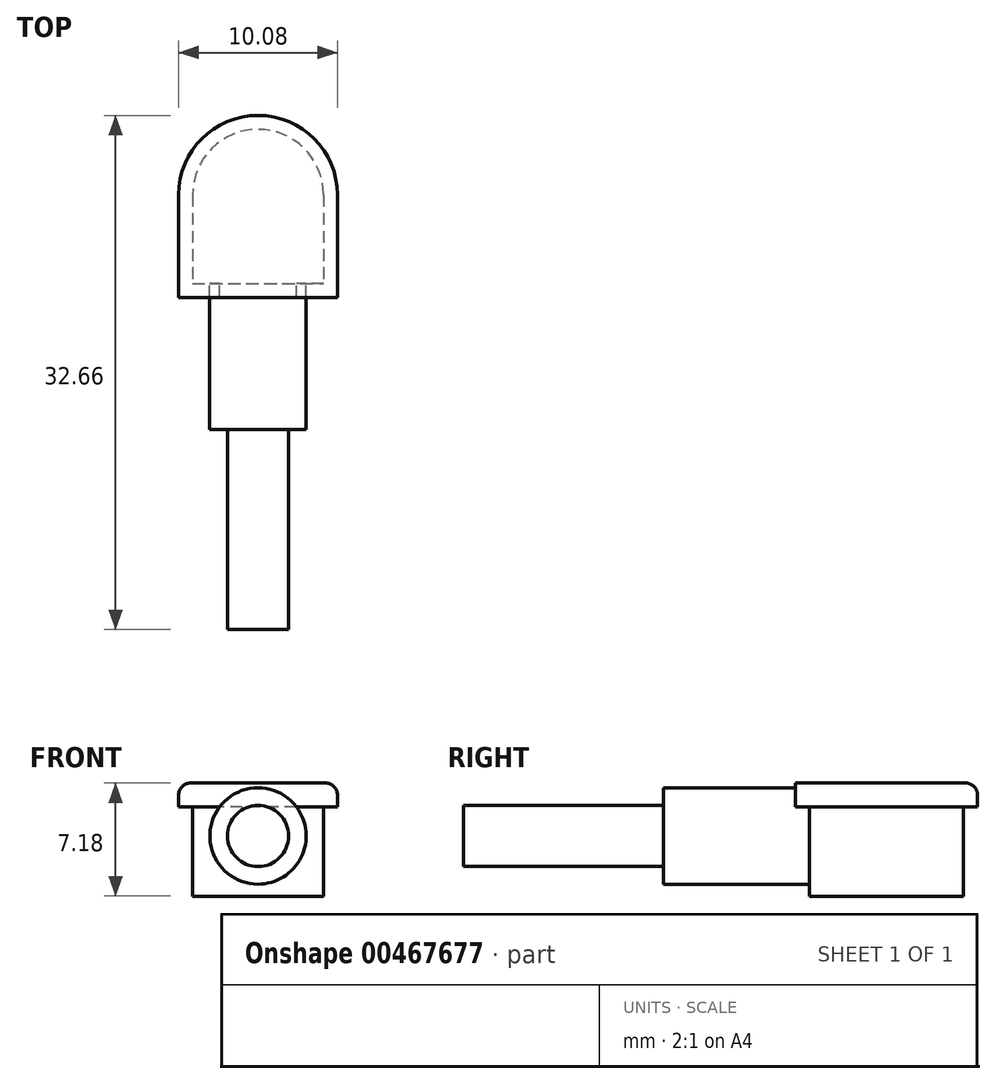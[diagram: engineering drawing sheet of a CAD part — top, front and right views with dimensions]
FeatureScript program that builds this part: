
annotation { "Feature Type Name" : "Feature", "Feature Type Description" : "" }
export const myFeature = defineFeature(function(context is Context, id is Id, definition is map)
    precondition{}
    {
        {
            var Q0;
            Q0=qCreatedBy(makeId("Top.planeOp"),FACE);
            var sketch = newSketch(context, id + "F0", { "sketchPlane" : qUnion([Q0])});
            skArc(sketch, "E0", {"start": v(4.15, 0) * mm, "mid": v(0, 4.15) * mm, "end": v(-4.15, 0) * mm});
            skLineSegment(sketch, "E1.top", {"start": v(-4.15, -5.63) * mm, "end": v(4.15, -5.63) * mm});
            skLineSegment(sketch, "E1.left", {"start": v(-4.15, 0) * mm, "end": v(-4.15, -5.63) * mm});
            skLineSegment(sketch, "E1.right", {"start": v(4.15, 0) * mm, "end": v(4.15, -5.63) * mm});
            skSolve(sketch);
        }
        {
            var Q0;
            Q0 = qSketchRegion(id + "F0", true);
            extrude(context, id + "F1", {"entities" : qUnion([Q0]), "oppositeDirection" : true, "depth" : 5.66 * mm});
        }
        {
            var Q0;
            Q0=makeQuery(id+"F1.opExtrude","CAP_FACE",FACE,{"disambiguationData":[OSD([sQuery(id+"F0.wireOp",EDGE,"E0"),sQuery(id+"F0.wireOp",EDGE,"E1.top"),sQuery(id+"F0.wireOp",EDGE,"E1.left"),sQuery(id+"F0.wireOp",EDGE,"E1.right")])],"isStart":true});
            var sketch = newSketch(context, id + "F2", { "sketchPlane" : qUnion([Q0])});
            skLineSegment(sketch, "E2.0.0", {"start": v(-4.15, 0) * mm, "end": v(-4.15, -5.63) * mm});
            skLineSegment(sketch, "E2.0.1", {"start": v(-4.15, -5.63) * mm, "end": v(4.15, -5.63) * mm});
            skLineSegment(sketch, "E2.0.2", {"start": v(4.15, -5.63) * mm, "end": v(4.15, 0) * mm});
            skArc(sketch, "E2.0.3", {"start": v(4.15, 0) * mm, "mid": v(0, 4.15) * mm, "end": v(-4.15, 0) * mm});
            skLineSegment(sketch, "E3.0", {"start": v(-5.04, 0) * mm, "end": v(-5.04, -6.52) * mm});
            skArc(sketch, "E3.1", {"start": v(5.04, 0) * mm, "mid": v(0, 5.04) * mm, "end": v(-5.04, 0) * mm});
            skLineSegment(sketch, "E3.2", {"start": v(5.04, -6.52) * mm, "end": v(5.04, 0) * mm});
            skLineSegment(sketch, "E3.3", {"start": v(-5.04, -6.52) * mm, "end": v(5.04, -6.52) * mm});
            skSolve(sketch);
        }
        {
            var Q0;
            Q0 = qSketchRegion(id + "F2", true);
            extrude(context, id + "F3", {"entities" : qUnion([Q0]), "operationType" : NewBodyOperationType.ADD, "depth" : 1.52 * mm});
        }
        {
            var Q0;
            Q0=makeQuery(id+"F1.opExtrude","CAP_FACE",FACE,{"disambiguationData":[OSD([sQuery(id+"F0.wireOp",EDGE,"E0"),sQuery(id+"F0.wireOp",EDGE,"E1.top"),sQuery(id+"F0.wireOp",EDGE,"E1.left"),sQuery(id+"F0.wireOp",EDGE,"E1.right")])],"isStart":true});
            var Q1;
            Q1=makeQuery(id+"F3.opExtrude","CAP_FACE",FACE,{"disambiguationData":[OSD([sQuery(id+"F2.wireOp",EDGE,"E2.0.0"),sQuery(id+"F2.wireOp",EDGE,"E2.0.1"),sQuery(id+"F2.wireOp",EDGE,"E2.0.2"),sQuery(id+"F2.wireOp",EDGE,"E2.0.3"),sQuery(id+"F2.wireOp",EDGE,"E3.0"),sQuery(id+"F2.wireOp",EDGE,"E3.1"),sQuery(id+"F2.wireOp",EDGE,"E3.2"),sQuery(id+"F2.wireOp",EDGE,"E3.3")])],"isStart":false});
            extrude(context, id + "F4", {"entities" : qUnion([Q0]), "endBound" : BoundingType.UP_TO_SURFACE, "endBoundEntityFace" : qUnion([Q1]), "depth" : 25.4 * mm});
        }
        {
            var Q0;
            Q0=makeQuery(id+"F1.opExtrude","SWEPT_FACE",FACE,{"disambiguationData":[OSD([sQuery(id+"F0.wireOp",EDGE,"E1.top")])]});
            var sketch = newSketch(context, id + "F5", { "sketchPlane" : qUnion([Q0])});
            skCircle(sketch, "E4", {"center": v(0, -1.84) * mm, "radius": 3.06 * mm});
            skSolve(sketch);
        }
        {
            var Q0;
            {var subQ0=sQuery(id+"F5.wireOp",EDGE,"E4");var subQ1=makeQuery(id+"F1.opExtrude","CAP_EDGE",EDGE,{"disambiguationData":[OSD([sQuery(id+"F0.wireOp",EDGE,"E1.top")])],"isStart":true});var subQ2=makeQuery(id+"F5.imprint","INTERSECT",VERTEX,{"disambiguationData":[OD(0.0)],"derivedFrom":[subQ1,subQ0]});Q0=makeQuery(id+"F5.imprint","IMPRINT",FACE,{"disambiguationData":[TD([[makeQuery(id+"F5.imprint","IMPRINT",EDGE,{"disambiguationData":[TD([[subQ2,-1.0]])],"derivedFrom":subQ0}),1.0]])]});}
            var Q1;
            {var subQ0=sQuery(id+"F5.wireOp",EDGE,"E4");var subQ1=makeQuery(id+"F1.opExtrude","CAP_EDGE",EDGE,{"disambiguationData":[OSD([sQuery(id+"F0.wireOp",EDGE,"E1.top")])],"isStart":true});var subQ2=makeQuery(id+"F5.imprint","INTERSECT",VERTEX,{"disambiguationData":[OD(0.0)],"derivedFrom":[subQ1,subQ0]});Q1=makeQuery(id+"F5.imprint","IMPRINT",FACE,{"disambiguationData":[TD([[makeQuery(id+"F5.imprint","IMPRINT",EDGE,{"disambiguationData":[TD([[subQ2,1.0]])],"derivedFrom":subQ0}),1.0]])]});}
            extrude(context, id + "F6", {"entities" : qUnion([Q0, Q1]), "operationType" : NewBodyOperationType.ADD, "depth" : 9.3 * mm});
        }
        {
            var Q0;
            Q0=makeQuery(id+"F3.opExtrude","CAP_EDGE",EDGE,{"disambiguationData":[OSD([sQuery(id+"F2.wireOp",EDGE,"E3.2")])],"isStart":false});
            fillet(context, id + "F7", {"entities" : qUnion([Q0]), "radius" : 0.76 * mm, "tangentPropagation" : true, "allowEdgeOverflow" : false});
        }
        {
            var Q0;
            Q0=makeQuery(id+"F6.opExtrude","CAP_FACE",FACE,{"disambiguationData":[OSD([sQuery(id+"F5.wireOp",EDGE,"E4")])],"isStart":false});
            var sketch = newSketch(context, id + "F8", { "sketchPlane" : qUnion([Q0])});
            skCircle(sketch, "E5", {"center": v(0, -1.84) * mm, "radius": 1.94 * mm});
            skSolve(sketch);
        }
        {
            var Q0;
            Q0=makeQuery(id+"F8.imprint","IMPRINT",FACE,{"disambiguationData":[TD([[makeQuery(id+"F8.imprint","IMPRINT",EDGE,{"derivedFrom":sQuery(id+"F8.wireOp",EDGE,"E5")}),1.0]])]});
            extrude(context, id + "F9", {"entities" : qUnion([Q0]), "operationType" : NewBodyOperationType.ADD, "depth" : 12.7 * mm});
        }
    });
